# Revit family: R 30 (a)
name_source: partatom
category: Equipement spécialisé
revit_build: Autodesk Revit LT 2015 (Build: 20140606_1530(x64)
units: mm (PartAtom-declared; Revit-internal decimal feet)

## types (5) — shared parameters
Apparent Power = 0 VA
Depth = 612 mm  [stored 2.00787 ft]
Description = CUTTERS VERTICAUX
Electrique connexion  Height = 177 mm  [stored 0.580709 ft]
Electrique connexion Depth = 412 mm  [stored 1.35171 ft]
Electrique connexion Width = 75 mm
Fabricant = ROBOT COUPE
Height = 1250 mm
Phase = 3
UP Depth = 750 mm
UP Height = 1698 mm  [stored 5.57087 ft]
UP Width = 773 mm
URL = www.robot-coupe.com
Waste water height = 720 mm
Width = 720 mm
water = Connector
zero-valued in all types: Cold water supply, Cold water supply height, Used water

## per-type parameters (varying)
| type | Amps | Cycle | Elec Conn RI Height | HP | Modèle | Speeds (Rpm) | Volts | Watts | Weight |
| R 30    400/50/3 | 20 A | 50 Hz | 0 mm  [stored 0 ft] |  | R 30 | 1500 & 3000 | 400 V | 5400 W | 148.4 kg |
| R 30    230/50/3 | 40 A | 50 Hz | 350 mm |  | R 30 | 1500 & 3000 | 230 V | 5400 W | 148.4 kg |
| R 30  USA   208-240/60/3 |  | 60 Hz | 0 mm  [stored 0 ft] | 7 | R 30 USA | 1800 & 3600 | 208 V | 0 W | 310 lbs |
| R 30    220/60/3 | 40 A | 60 Hz | 350 mm |  | R 30 | 1500 & 3000 | 220 V | 5400 W | 148.4 kg |
| R 30    380/60/3 | 20 A | 60 Hz | 0 mm  [stored 0 ft] |  | R 30 | 1500 & 3000 | 380 V | 5400 W | 148.4 kg |

note: [stored X ft] marks values corroborated as IEEE doubles in the binary element streams (Revit-internal decimal feet)

## geometry (parser evidence)
native form markers: Blend x85, Sweep x5
no freeform markers — native parametric forms only
